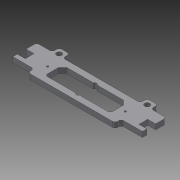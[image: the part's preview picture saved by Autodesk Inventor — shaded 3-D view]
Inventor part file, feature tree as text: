
AUTODESK INVENTOR PART (.ipt)
format: ipt  version: 2016 (Build 200138000, 138)  size: 198,656 bytes
history: native  units: mm
features: extrude x8, sketch x8, chamfer x2, mirror x1, fillet x1
ambient origin geometry x8: Origin, YZ Plane, XZ Plane, XY Plane, X Axis, Y Axis, Z Axis, Center Point
bodies: Solid1 (feature_tree)
feature tree (20):
  extrude  "Extrusion1"  Depth=34.0mm
  extrude  "Extrusion2"  Depth=74.0mm
  extrude  "Extrusion3"  Depth=6.0mm TaperAngle=0.0deg
  extrude  "Extrusion4"  Depth=9.0mm
  extrude  "Extrusion5"  Depth=9.0mm
  extrude  "Extrusion6"  Depth=6.0mm
  extrude  "Extrusion7"  Depth=12.0mm
  mirror  "Mirror1"
  chamfer  "Chamfer3"  Distance=2.0mm
  chamfer  "Chamfer4"  Distance=6.0mm
  fillet  "Fillet2"  Radius=9.0mm
  extrude  "Extrusion8"  Depth=10.0mm
  sketch  "Sketch1"  dims[d0=147.0mm d1=34.0mm]
  sketch  "Sketch2"  dims[d2=6.0mm d3=0.0mm d4=74.0mm]
  sketch  "Sketch3"  dims[d5=20.0mm d6=6.0mm d7=0.0mm]
  sketch  "Sketch4"  dims[d8=5.0mm d10=9.0mm]
  sketch  "Sketch5"  dims[d11=5.0mm d12=9.0mm]
  sketch  "Sketch6"  dims[d13=6.0mm d14=0.0mm d15=6.0mm]
  sketch  "Sketch7"  dims[d16=12.0mm d17=12.0mm]
  sketch  "Sketch8"  dims[d18=50.0mm d19=2.0mm d20=6.0mm d21=0.0mm d22=9.0mm d23=10.0mm d24=6.0mm d25=0.0mm d26=24.0mm d28=7.0mm d29=6.0mm d30=0.0mm d31=2.25mm d32=44.1mm d33=6.0mm d34=0.0mm d42=5.0mm d43=2.0mm d44=45.0deg d45=2.0mm d46=2.0mm d47=45.0deg d48=3.0mm d49=10.0mm d50=0.0mm]
